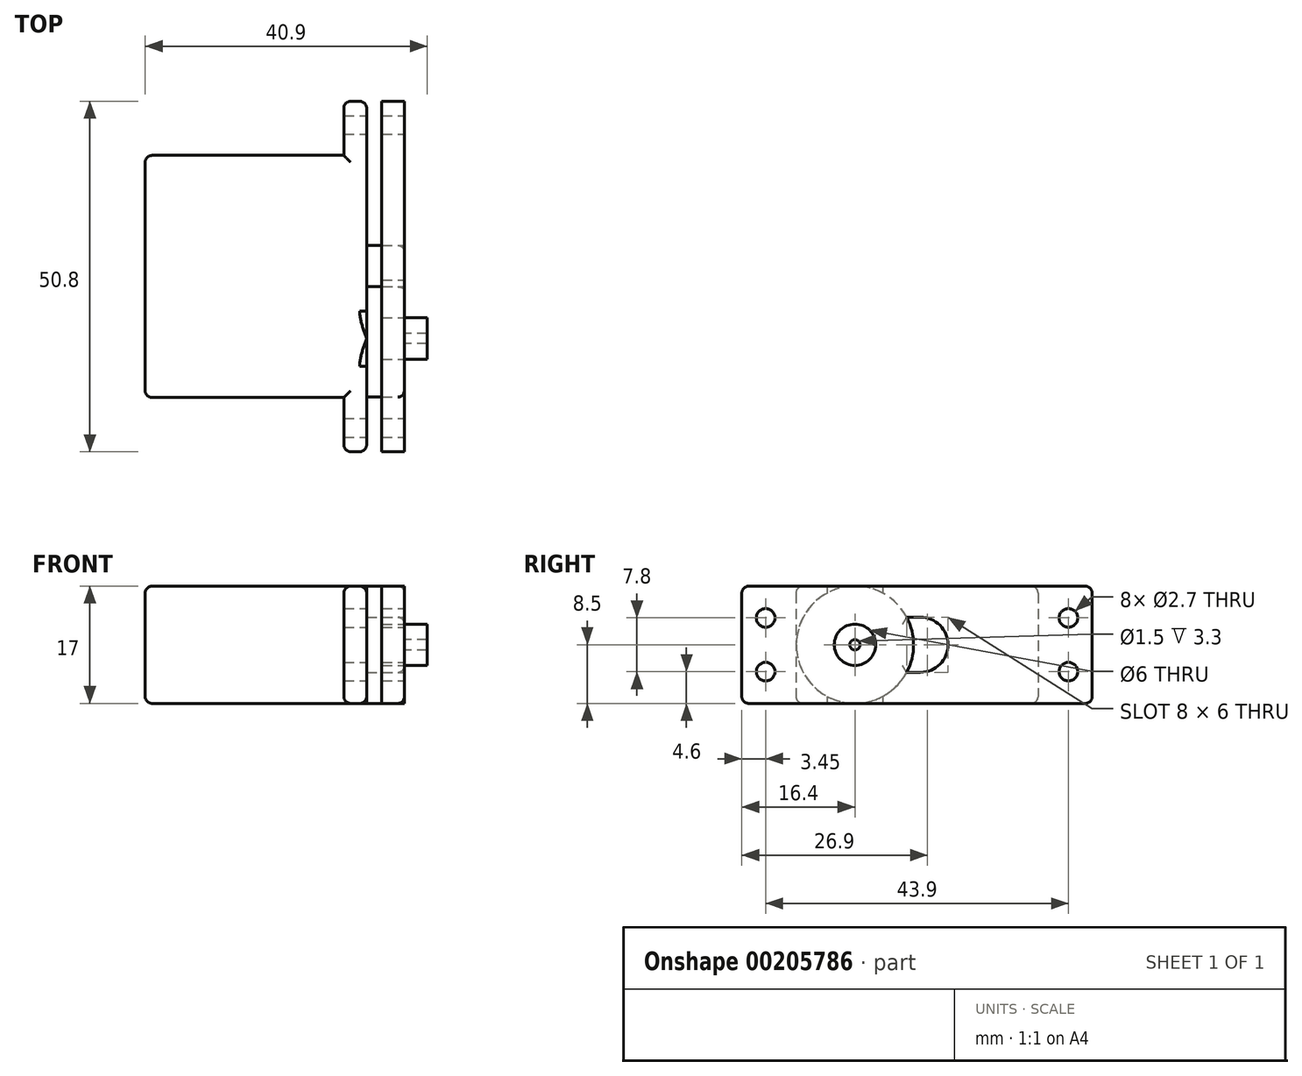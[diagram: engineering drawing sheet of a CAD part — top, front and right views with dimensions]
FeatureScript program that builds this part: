
annotation { "Feature Type Name" : "Feature", "Feature Type Description" : "" }
export const myFeature = defineFeature(function(context is Context, id is Id, definition is map)
    precondition{}
    {
        {
            var Q0;
            Q0=qCreatedBy(makeId("Top.planeOp"),FACE);
            var sketch = newSketch(context, id + "F0", { "sketchPlane" : qUnion([Q0])});
            skLineSegment(sketch, "E0", {"start": v(-10, 0) * mm, "end": v(10, 0) * mm});
            skSolve(sketch);
        }
        {
            var Q0;
            Q0=sQuery(id+"F0.wireOp",VERTEX,"E0.start");
            var Q1;
            Q1=sQuery(id+"F0.wireOp",EDGE,"E0");
            cPlane(context, id + "F1", {"entities" : qUnion([Q0, Q1]), "cplaneType" : CPlaneType.LINE_POINT, "offset" : 25 * mm, "width" : 150 * mm, "height" : 150 * mm});
        }
        {
            var Q0;
            Q0=qCreatedBy(id+"F1.planeOp",FACE);
            var sketch = newSketch(context, id + "F2", { "sketchPlane" : qUnion([Q0])});
            skLineSegment(sketch, "E1.bottom", {"start": v(-15.4, 8.5) * mm, "end": v(33.4, 8.5) * mm});
            skLineSegment(sketch, "E1.top", {"start": v(-15.4, -8.5) * mm, "end": v(33.4, -8.5) * mm});
            skLineSegment(sketch, "E1.left", {"start": v(-16.4, 7.5) * mm, "end": v(-16.4, -7.5) * mm});
            skLineSegment(sketch, "E1.right", {"start": v(34.4, 7.5) * mm, "end": v(34.4, -7.5) * mm});
            skLineSegment(sketch, "E2", {"start": v(0, 8.5) * mm, "end": v(0, -8.5) * mm, "construction": true});
            skCircle(sketch, "E3", {"center": v(-12.95, 3.9) * mm, "radius": 1.35 * mm});
            skLineSegment(sketch, "E4", {"start": v(-16.4, 0) * mm, "end": v(34.4, 0) * mm, "construction": true});
            skCircle(sketch, "E5.MirrorC", {"center": v(-12.95, -3.9) * mm, "radius": 1.35 * mm});
            skLineSegment(sketch, "E6", {"start": v(-12.95, 3.9) * mm, "end": v(-12.95, -3.9) * mm, "construction": true});
            skLineSegment(sketch, "E7", {"start": v(9, 8.5) * mm, "end": v(9, -8.5) * mm, "construction": true});
            skCircle(sketch, "E8.MirrorC", {"center": v(30.95, 3.9) * mm, "radius": 1.35 * mm});
            skLineSegment(sketch, "E9.MirrorCS", {"start": v(30.95, 3.9) * mm, "end": v(30.95, -3.9) * mm, "construction": true});
            skCircle(sketch, "E10.MirrorC", {"center": v(30.95, -3.9) * mm, "radius": 1.35 * mm});
            skPoint(sketch, "E11.visualSharp", {"position": v(-16.4, 8.5) * mm});
            skArc(sketch, "E11.filletArc", {"start": v(-15.4, 8.5) * mm, "mid": v(-16.1, 8.2) * mm, "end": v(-16.4, 7.5) * mm});
            skPoint(sketch, "E12.visualSharp", {"position": v(-16.4, -8.5) * mm});
            skArc(sketch, "E12.filletArc", {"start": v(-16.4, -7.5) * mm, "mid": v(-16.1, -8.2) * mm, "end": v(-15.4, -8.5) * mm});
            skPoint(sketch, "E13.visualSharp", {"position": v(34.4, -8.5) * mm});
            skArc(sketch, "E13.filletArc", {"start": v(33.4, -8.5) * mm, "mid": v(34.1, -8.2) * mm, "end": v(34.4, -7.5) * mm});
            skPoint(sketch, "E14.visualSharp", {"position": v(34.4, 8.5) * mm});
            skArc(sketch, "E14.filletArc", {"start": v(34.4, 7.5) * mm, "mid": v(34.1, 8.2) * mm, "end": v(33.4, 8.5) * mm});
            skCircle(sketch, "E15", {"center": v(0, 0) * mm, "radius": 8.5 * mm});
            skArc(sketch, "E16", {"start": v(9.5, -4) * mm, "mid": v(13.5, 0) * mm, "end": v(9.5, 4) * mm});
            skPoint(sketch, "E17", {"position": v(13.5, 0) * mm});
            skPoint(sketch, "E18", {"position": v(-8.5, 0) * mm});
            skLineSegment(sketch, "E19", {"start": v(9.5, 4) * mm, "end": v(7.5, 4) * mm});
            skLineSegment(sketch, "E20.MirrorCS", {"start": v(9.5, -4) * mm, "end": v(7.5, -4) * mm});
            skCircle(sketch, "E21", {"center": v(0, 0) * mm, "radius": 3 * mm});
            skCircle(sketch, "E22", {"center": v(0, 0) * mm, "radius": 0.75 * mm});
            skLineSegment(sketch, "E23", {"start": v(-8.55, 8.5) * mm, "end": v(-8.55, -8.5) * mm});
            skLineSegment(sketch, "E24.MirrorCS", {"start": v(26.55, 8.5) * mm, "end": v(26.55, -8.5) * mm});
            skSolve(sketch);
        }
        {
            var Q0;
            Q0=qCreatedBy(id+"F1.planeOp",FACE);
            var sketch = newSketch(context, id + "F3", { "sketchPlane" : qUnion([Q0])});
            skCircle(sketch, "E25.0", {"center": v(0, 0) * mm, "radius": 8.5 * mm});
            skLineSegment(sketch, "E26.0", {"start": v(9.5, 4) * mm, "end": v(7.5, 4) * mm});
            skArc(sketch, "E27.0", {"start": v(9.5, -4) * mm, "mid": v(13.5, 0) * mm, "end": v(9.5, 4) * mm});
            skLineSegment(sketch, "E28.0", {"start": v(9.5, -4) * mm, "end": v(7.5, -4) * mm});
            skSolve(sketch);
        }
        {
            var Q0;
            Q0=qSketchRegion(id+"F3",true);
            extrude(context, id + "F4", {"entities" : qUnion([Q0]), "oppositeDirection" : true, "depth" : 5.5 * mm});
        }
        {
            var Q0;
            Q0=makeQuery(id+"F4.opExtrude","CAP_FACE",FACE,{"disambiguationData":[OSD([sQuery(id+"F3.wireOp",EDGE,"E25.0"),sQuery(id+"F3.wireOp",EDGE,"E26.0"),sQuery(id+"F3.wireOp",EDGE,"E27.0"),sQuery(id+"F3.wireOp",EDGE,"E28.0")])],"isStart":false});
            var sketch = newSketch(context, id + "F5", { "sketchPlane" : qUnion([Q0])});
            skLineSegment(sketch, "E29.0", {"start": v(16.4, 7.5) * mm, "end": v(16.4, -7.5) * mm});
            skLineSegment(sketch, "E30.0", {"start": v(15.4, 8.5) * mm, "end": v(-33.4, 8.5) * mm});
            skPoint(sketch, "E31.0", {"position": v(16.4, 8.5) * mm});
            skPoint(sketch, "E32.0", {"position": v(15.4, 7.5) * mm});
            skArc(sketch, "E33.0", {"start": v(15.4, 8.5) * mm, "mid": v(16.1, 8.2) * mm, "end": v(16.4, 7.5) * mm});
            skPoint(sketch, "E34.0", {"position": v(16.4, -8.5) * mm});
            skPoint(sketch, "E35.0", {"position": v(15.4, -7.5) * mm});
            skLineSegment(sketch, "E36.0.1", {"start": v(0, 8.5) * mm, "end": v(15.4, 8.5) * mm});
            skArc(sketch, "E36.0.4", {"start": v(16.4, -7.5) * mm, "mid": v(16.1, -8.2) * mm, "end": v(15.4, -8.5) * mm});
            skLineSegment(sketch, "E36.0.5", {"start": v(15.4, -8.5) * mm, "end": v(0, -8.5) * mm});
            skLineSegment(sketch, "E37.0.5", {"start": v(0, -8.5) * mm, "end": v(-33.4, -8.5) * mm});
            skArc(sketch, "E37.0.6", {"start": v(-33.4, -8.5) * mm, "mid": v(-34.1, -8.2) * mm, "end": v(-34.4, -7.5) * mm});
            skLineSegment(sketch, "E37.0.7", {"start": v(-34.4, -7.5) * mm, "end": v(-34.4, 7.5) * mm});
            skArc(sketch, "E37.0.8", {"start": v(-34.4, 7.5) * mm, "mid": v(-34.1, 8.2) * mm, "end": v(-33.4, 8.5) * mm});
            skLineSegment(sketch, "E37.0.9", {"start": v(-33.4, 8.5) * mm, "end": v(0, 8.5) * mm});
            skCircle(sketch, "E38.0", {"center": v(-30.95, -3.9) * mm, "radius": 1.35 * mm});
            skCircle(sketch, "E39.0", {"center": v(-30.95, 3.9) * mm, "radius": 1.35 * mm});
            skCircle(sketch, "E40.0", {"center": v(12.95, -3.9) * mm, "radius": 1.35 * mm});
            skCircle(sketch, "E41.0", {"center": v(12.95, 3.9) * mm, "radius": 1.35 * mm});
            skSolve(sketch);
        }
        {
            var Q0;
            Q0=qSketchRegion(id+"F5",true);
            extrude(context, id + "F6", {"entities" : qUnion([Q0]), "operationType" : NewBodyOperationType.ADD, "depth" : 3.3 * mm});
        }
        {
            var Q0;
            Q0=makeQuery(id+"F6.opExtrude","CAP_FACE",FACE,{"disambiguationData":[OSD([sQuery(id+"F5.wireOp",EDGE,"E36.0.1"),sQuery(id+"F5.wireOp",EDGE,"E33.0"),sQuery(id+"F5.wireOp",EDGE,"E29.0"),sQuery(id+"F5.wireOp",EDGE,"E36.0.4"),sQuery(id+"F5.wireOp",EDGE,"E36.0.5"),sQuery(id+"F5.wireOp",EDGE,"E37.0.5"),sQuery(id+"F5.wireOp",EDGE,"E37.0.6"),sQuery(id+"F5.wireOp",EDGE,"E37.0.7"),sQuery(id+"F5.wireOp",EDGE,"E37.0.8"),sQuery(id+"F5.wireOp",EDGE,"E37.0.9"),sQuery(id+"F5.wireOp",EDGE,"E38.0"),sQuery(id+"F5.wireOp",EDGE,"E39.0"),sQuery(id+"F5.wireOp",EDGE,"E40.0"),sQuery(id+"F5.wireOp",EDGE,"E41.0")])],"isStart":false});
            var sketch = newSketch(context, id + "F7", { "sketchPlane" : qUnion([Q0])});
            skLineSegment(sketch, "E42.0", {"start": v(8.55, 7.5) * mm, "end": v(8.55, -7.5) * mm});
            skLineSegment(sketch, "E43.0", {"start": v(-26.55, 7.5) * mm, "end": v(-26.55, -7.5) * mm});
            skLineSegment(sketch, "E44", {"start": v(7.55, -8.5) * mm, "end": v(-25.55, -8.5) * mm});
            skLineSegment(sketch, "E45", {"start": v(7.55, 8.5) * mm, "end": v(-25.55, 8.5) * mm});
            skPoint(sketch, "E46.visualSharp", {"position": v(8.55, 8.5) * mm});
            skArc(sketch, "E46.filletArc", {"start": v(8.55, 7.5) * mm, "mid": v(8.26, 8.2) * mm, "end": v(7.55, 8.5) * mm});
            skPoint(sketch, "E47.visualSharp", {"position": v(8.55, -8.5) * mm});
            skArc(sketch, "E47.filletArc", {"start": v(7.55, -8.5) * mm, "mid": v(8.26, -8.2) * mm, "end": v(8.55, -7.5) * mm});
            skPoint(sketch, "E48.visualSharp", {"position": v(-26.55, -8.5) * mm});
            skArc(sketch, "E48.filletArc", {"start": v(-26.55, -7.5) * mm, "mid": v(-26.26, -8.2) * mm, "end": v(-25.55, -8.5) * mm});
            skPoint(sketch, "E49.visualSharp", {"position": v(-26.55, 8.5) * mm});
            skArc(sketch, "E49.filletArc", {"start": v(-25.55, 8.5) * mm, "mid": v(-26.26, 8.2) * mm, "end": v(-26.55, 7.5) * mm});
            skSolve(sketch);
        }
        {
            var Q0;
            Q0=qSketchRegion(id+"F7",true);
            extrude(context, id + "F8", {"entities" : qUnion([Q0]), "operationType" : NewBodyOperationType.ADD, "depth" : 28.8 * mm});
        }
        {
            var Q0;
            Q0=makeQuery(id+"F8.opExtrude","CAP_EDGE",EDGE,{"disambiguationData":[OSD([sQuery(id+"F7.wireOp",EDGE,"E42.0")])],"isStart":false});
            var Q1;
            Q1=makeQuery(id+"F8.opExtrude","CAP_EDGE",EDGE,{"disambiguationData":[OSD([sQuery(id+"F7.wireOp",EDGE,"E42.0")])],"isStart":true});
            var Q2;
            Q2=makeQuery(id+"F8.opExtrude","CAP_EDGE",EDGE,{"disambiguationData":[OSD([sQuery(id+"F7.wireOp",EDGE,"E43.0")])],"isStart":true});
            var Q3;
            Q3=makeQuery(id+"F6.opExtrude","CAP_EDGE",EDGE,{"disambiguationData":[OSD([sQuery(id+"F5.wireOp",EDGE,"E37.0.7")])],"isStart":false});
            var Q4;
            Q4=makeQuery(id+"F6.opExtrude","CAP_EDGE",EDGE,{"disambiguationData":[OSD([sQuery(id+"F5.wireOp",EDGE,"E37.0.7")])],"isStart":true});
            var Q5;
            Q5=makeQuery(id+"F6.opExtrude","CAP_EDGE",EDGE,{"disambiguationData":[OSD([sQuery(id+"F5.wireOp",EDGE,"E33.0")])],"isStart":false});
            var Q6;
            Q6=makeQuery(id+"F4.opExtrude","CAP_EDGE",EDGE,{"disambiguationData":[OSD([sQuery(id+"F3.wireOp",EDGE,"E25.0")])],"isStart":true});
            var Q7;
            Q7=makeQuery(id+"F4.opExtrude","CAP_EDGE",EDGE,{"disambiguationData":[OSD([sQuery(id+"F3.wireOp",EDGE,"E27.0")])],"isStart":true});
            fillet(context, id + "F9", {"entities" : qUnion([Q0, Q1, Q2, Q3, Q4, Q5, Q6, Q7]), "radius" : 1 * mm, "tangentPropagation" : true, "allowEdgeOverflow" : false});
        }
        {
            var Q0;
            Q0=makeQuery(id+"F2.imprint","IMPRINT",FACE,{"disambiguationData":[TD([[makeQuery(id+"F2.imprint","IMPRINT",EDGE,{"derivedFrom":sQuery(id+"F2.wireOp",EDGE,"E21")}),1.0]])]});
            extrude(context, id + "F10", {"entities" : qUnion([Q0]), "operationType" : NewBodyOperationType.ADD, "depth" : 3.3 * mm});
        }
        {
            var Q0;
            Q0=qSketchRegion(id+"F2",true);
            extrude(context, id + "F11", {"entities" : qUnion([Q0]), "oppositeDirection" : true, "depth" : 3.3 * mm});
        }
    });
